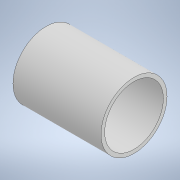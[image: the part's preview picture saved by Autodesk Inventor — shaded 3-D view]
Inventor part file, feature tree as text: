
AUTODESK INVENTOR PART (.ipt)
format: ipt  version: 2022 (Build 260153000, 153)  size: 114,176 bytes
history: native  units: in
note: dims shown in document units (in); Inventor stores cm internally (conversion verified against a paired STEP export)
features: extrude x1, sketch x1, other x1
ambient origin geometry x8: Origin, YZ Plane, XZ Plane, XY Plane, X Axis, Y Axis, Z Axis, Center Point
bodies: Solid1 (feature_tree)
feature tree (3):
  extrude  "Extrusion1"  [1 undecoded]
  sketch  "Sketch2"  dims[d0=57.0in d1=0.0in]
  other  "Boss-Extrude2"
note: 1 required parameter value undecoded (feature->parameter linkage not recoverable at this tier; creation-order binding heuristic only, values carry confidence <= 0.55)
